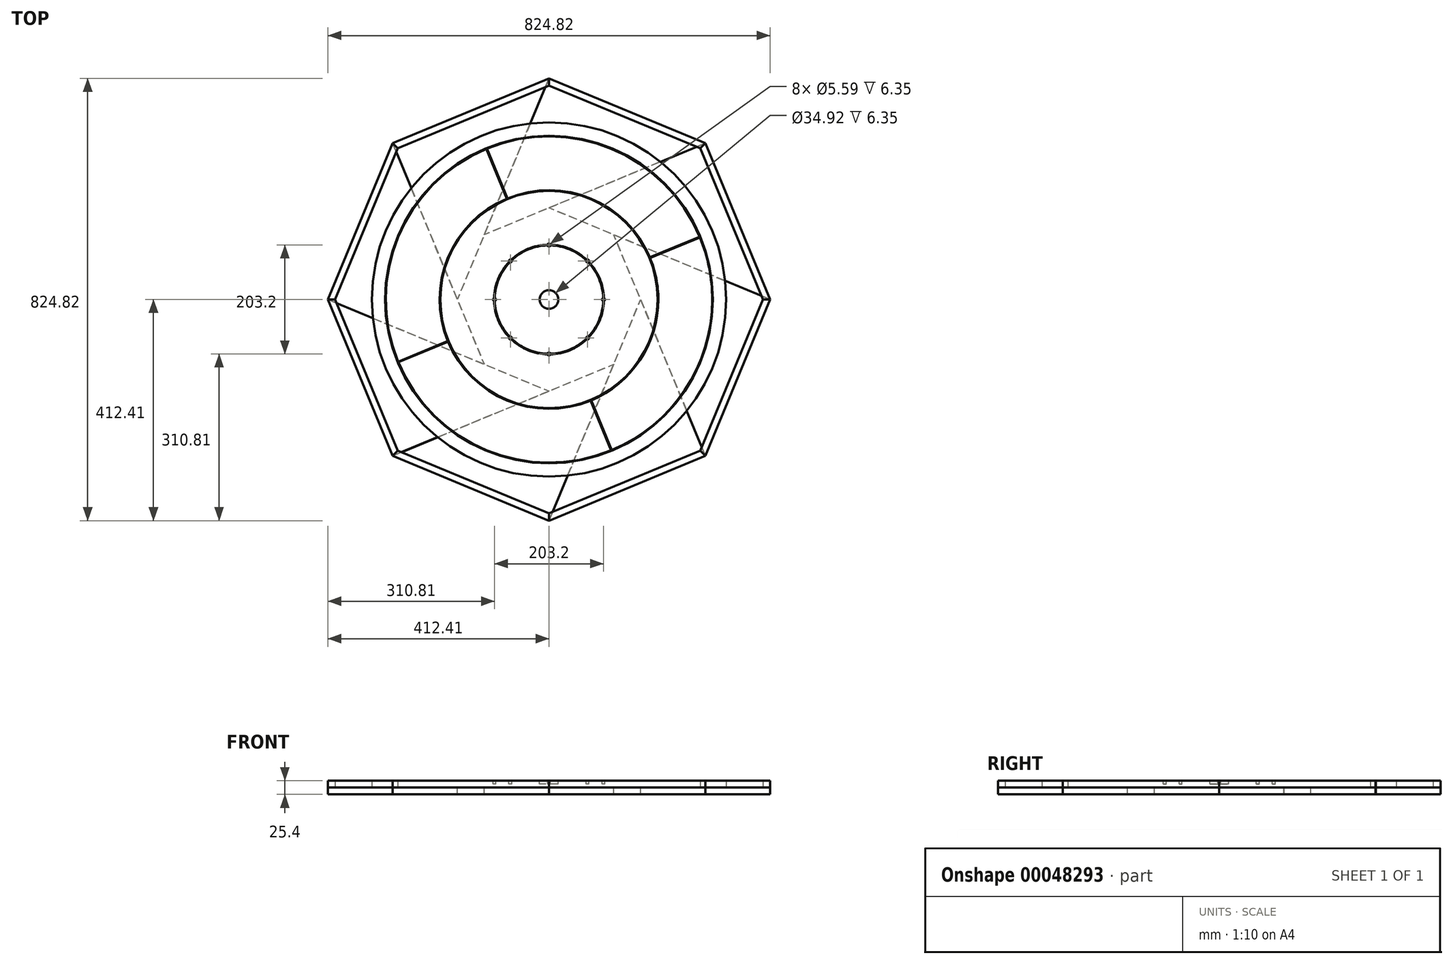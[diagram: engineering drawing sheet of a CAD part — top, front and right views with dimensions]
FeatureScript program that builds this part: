
annotation { "Feature Type Name" : "Feature", "Feature Type Description" : "" }
export const myFeature = defineFeature(function(context is Context, id is Id, definition is map)
    precondition{}
    {
        {
            var Q0;
            Q0=qCreatedBy(makeId("Top.planeOp"),FACE);
            var sketch = newSketch(context, id + "F0", { "sketchPlane" : qUnion([Q0])});
            skCircle(sketch, "E0", {"center": v(0, 0) * mm, "radius": 330.2 * mm});
            skSolve(sketch);
        }
        {
            var Q0;
            Q0=makeQuery(id+"F0.imprint","IMPRINT",FACE,{"disambiguationData":[TD([[makeQuery(id+"F0.imprint","IMPRINT",EDGE,{"derivedFrom":sQuery(id+"F0.wireOp",EDGE,"E0")}),1.0]])]});
            extrude(context, id + "F1", {"entities" : qUnion([Q0]), "depth" : 12.7 * mm});
        }
        {
            var Q0;
            Q0=makeQuery(id+"F1.opExtrude","CAP_FACE",FACE,{"disambiguationData":[OSD([sQuery(id+"F0.wireOp",EDGE,"E0")])],"isStart":false});
            var sketch = newSketch(context, id + "F2", { "sketchPlane" : qUnion([Q0])});
            skCircle(sketch, "E1", {"center": v(0, 0) * mm, "radius": 17.46 * mm});
            skSolve(sketch);
        }
        {
            var Q0;
            Q0 = qSketchRegion(id + "F2", true);
            extrude(context, id + "F3", {"entities" : qUnion([Q0]), "operationType" : NewBodyOperationType.REMOVE, "oppositeDirection" : true, "depth" : 6.35 * mm});
        }
        {
            var Q0;
            Q0=makeQuery(id+"F1.opExtrude","CAP_FACE",FACE,{"disambiguationData":[OSD([sQuery(id+"F0.wireOp",EDGE,"E0")])],"isStart":false});
            var sketch = newSketch(context, id + "F4", { "sketchPlane" : qUnion([Q0])});
            skCircle(sketch, "E2", {"center": v(101.6, 0) * mm, "radius": 2.8 * mm});
            skCircle(sketch, "E3.1.0", {"center": v(71.84, 71.84) * mm, "radius": 2.8 * mm});
            skCircle(sketch, "E3.2.0", {"center": v(0, 101.6) * mm, "radius": 2.8 * mm});
            skCircle(sketch, "E3.3.0", {"center": v(-71.84, 71.84) * mm, "radius": 2.8 * mm});
            skCircle(sketch, "E3.4.0", {"center": v(-101.6, 0) * mm, "radius": 2.8 * mm});
            skCircle(sketch, "E3.5.0", {"center": v(-71.84, -71.84) * mm, "radius": 2.8 * mm});
            skCircle(sketch, "E3.6.0", {"center": v(0, -101.6) * mm, "radius": 2.8 * mm});
            skCircle(sketch, "E3.7.0", {"center": v(71.84, -71.84) * mm, "radius": 2.8 * mm});
            skPoint(sketch, "E3.center", {"position": v(0, 0) * mm});
            skSolve(sketch);
        }
        {
            var Q0;
            Q0 = qSketchRegion(id + "F4", true);
            extrude(context, id + "F5", {"entities" : qUnion([Q0]), "operationType" : NewBodyOperationType.REMOVE, "oppositeDirection" : true, "depth" : 6.35 * mm});
        }
        {
            var Q0;
            Q0=qCreatedBy(makeId("Front.planeOp"),FACE);
            var sketch = newSketch(context, id + "F6", { "sketchPlane" : qUnion([Q0])});
            skArc(sketch, "E4", {"start": v(-102.24, 12.7) * mm, "mid": v(-101.6, 12.53) * mm, "end": v(-100.97, 12.7) * mm});
            skLineSegment(sketch, "E5", {"start": v(-102.24, 12.7) * mm, "end": v(-100.97, 12.7) * mm});
            skLineSegment(sketch, "E6", {"start": v(0, 0) * mm, "end": v(0, 26.45) * mm});
            skLineSegment(sketch, "E7.1.0.0", {"start": v(-203.84, 12.7) * mm, "end": v(-202.57, 12.7) * mm});
            skArc(sketch, "E7.1.0.1", {"start": v(-203.84, 12.7) * mm, "mid": v(-203.2, 12.53) * mm, "end": v(-202.57, 12.7) * mm});
            skLineSegment(sketch, "E7.direction1", {"start": v(-102.24, 12.7) * mm, "end": v(-203.84, 12.7) * mm, "construction": true});
            skLineSegment(sketch, "E8.0.2.0", {"start": v(-305.44, 12.7) * mm, "end": v(-304.17, 12.7) * mm});
            skArc(sketch, "E8.3.2.0", {"start": v(-305.44, 12.7) * mm, "mid": v(-304.8, 12.53) * mm, "end": v(-304.17, 12.7) * mm});
            skSolve(sketch);
        }
        {
            var Q0;
            Q0 = qSketchRegion(id + "F6", true);
            var Q1;
            Q1=sQuery(id+"F6.wireOp",EDGE,"E6");
            revolve(context, id + "F7", {"operationType" : NewBodyOperationType.REMOVE, "entities" : qUnion([Q0]), "axis" : qUnion([Q1]), "revolveType" : RevolveType.FULL, "oppositeDirection" : true});
        }
        {
            var Q0;
            Q0=makeQuery(id+"F5.boolean.opBoolean","COPY",FACE,{"derivedFrom":makeQuery(id+"F5.opExtrude","SWEPT_FACE",FACE,{"disambiguationData":[OSD([sQuery(id+"F4.wireOp",EDGE,"E3.3.0")])]})});
            var Q1;
            Q1=makeQuery(id+"F5.boolean.opBoolean","COPY",FACE,{"derivedFrom":makeQuery(id+"F5.opExtrude","SWEPT_FACE",FACE,{"disambiguationData":[OSD([sQuery(id+"F4.wireOp",EDGE,"E3.2.0")])]})});
            cPlane(context, id + "F8", {"entities" : qUnion([Q0, Q1]), "cplaneType" : CPlaneType.LINE_ANGLE, "offset" : 152.4 * mm, "angle" : 0 * degree, "width" : 152.4 * mm, "height" : 152.4 * mm});
        }
        {
            var Q0;
            Q0=makeQuery(id+"F7.boolean.opBoolean","SPLIT",FACE,{"disambiguationData":[TD([makeQuery(id+"F3.boolean.opBoolean","COPY",FACE,{"derivedFrom":makeQuery(id+"F3.opExtrude","SWEPT_FACE",FACE,{"disambiguationData":[OSD([sQuery(id+"F2.wireOp",EDGE,"E1")])]})}),makeQuery(id+"F5.boolean.opBoolean","COPY",FACE,{"derivedFrom":makeQuery(id+"F5.opExtrude","SWEPT_FACE",FACE,{"disambiguationData":[OSD([sQuery(id+"F4.wireOp",EDGE,"E2")])]})}),makeQuery(id+"F5.boolean.opBoolean","COPY",FACE,{"derivedFrom":makeQuery(id+"F5.opExtrude","SWEPT_FACE",FACE,{"disambiguationData":[OSD([sQuery(id+"F4.wireOp",EDGE,"E3.1.0")])]})}),makeQuery(id+"F5.boolean.opBoolean","COPY",FACE,{"derivedFrom":makeQuery(id+"F5.opExtrude","SWEPT_FACE",FACE,{"disambiguationData":[OSD([sQuery(id+"F4.wireOp",EDGE,"E3.2.0")])]})}),makeQuery(id+"F5.boolean.opBoolean","COPY",FACE,{"derivedFrom":makeQuery(id+"F5.opExtrude","SWEPT_FACE",FACE,{"disambiguationData":[OSD([sQuery(id+"F4.wireOp",EDGE,"E3.3.0")])]})}),makeQuery(id+"F5.boolean.opBoolean","COPY",FACE,{"derivedFrom":makeQuery(id+"F5.opExtrude","SWEPT_FACE",FACE,{"disambiguationData":[OSD([sQuery(id+"F4.wireOp",EDGE,"E3.4.0")])]})}),makeQuery(id+"F5.boolean.opBoolean","COPY",FACE,{"derivedFrom":makeQuery(id+"F5.opExtrude","SWEPT_FACE",FACE,{"disambiguationData":[OSD([sQuery(id+"F4.wireOp",EDGE,"E3.5.0")])]})}),makeQuery(id+"F5.boolean.opBoolean","COPY",FACE,{"derivedFrom":makeQuery(id+"F5.opExtrude","SWEPT_FACE",FACE,{"disambiguationData":[OSD([sQuery(id+"F4.wireOp",EDGE,"E3.6.0")])]})}),makeQuery(id+"F5.boolean.opBoolean","COPY",FACE,{"derivedFrom":makeQuery(id+"F5.opExtrude","SWEPT_FACE",FACE,{"disambiguationData":[OSD([sQuery(id+"F4.wireOp",EDGE,"E3.7.0")])]})}),makeQuery(id+"F7.opRevolve","SWEPT_FACE",FACE,{"disambiguationData":[OSD([sQuery(id+"F6.wireOp",EDGE,"E4")])]})])],"derivedFrom":makeQuery(id+"F1.opExtrude","CAP_FACE",FACE,{"disambiguationData":[OSD([sQuery(id+"F0.wireOp",EDGE,"E0")])],"isStart":false})});
            var sketch = newSketch(context, id + "F9", { "sketchPlane" : qUnion([Q0])});
            skLineSegment(sketch, "E9", {"start": v(0, 0) * mm, "end": v(-110.78, 267.45) * mm});
            skLineSegment(sketch, "E10", {"start": v(-78, 188.32) * mm, "end": v(-110.7, 174.78) * mm});
            skLineSegment(sketch, "E11", {"start": v(-78, 188.32) * mm, "end": v(-71.84, 71.84) * mm});
            skLineSegment(sketch, "E12", {"start": v(0, 101.6) * mm, "end": v(-78, 188.32) * mm});
            skSolve(sketch);
        }
        {
            var Q0;
            Q0=qCreatedBy(id+"F8.planeOp",FACE);
            var Q1;
            Q1=sQuery(id+"F9.wireOp",VERTEX,"E10.end");
            cPlane(context, id + "F10", {"entities" : qUnion([Q0, Q1]), "cplaneType" : CPlaneType.PLANE_POINT, "offset" : 152.4 * mm, "width" : 152.4 * mm, "height" : 152.4 * mm});
        }
        {
            var Q0;
            Q0=qCreatedBy(id+"F10.planeOp",FACE);
            var sketch = newSketch(context, id + "F11", { "sketchPlane" : qUnion([Q0])});
            skArc(sketch, "E13", {"start": v(-0.63, 12.7) * mm, "mid": v(0, 12.53) * mm, "end": v(0.64, 12.7) * mm});
            skLineSegment(sketch, "E14", {"start": v(-0.63, 12.7) * mm, "end": v(0.64, 12.7) * mm});
            skSolve(sketch);
        }
        {
            var Q0;
            Q0 = qSketchRegion(id + "F11", true);
            extrude(context, id + "F12", {"entities" : qUnion([Q0]), "operationType" : NewBodyOperationType.REMOVE, "oppositeDirection" : true, "depth" : 100.56 * mm});
        }
        {
            var Q0;
            Q0=makeQuery(id+"F12.boolean.opBoolean","COPY",FACE,{"derivedFrom":makeQuery(id+"F12.opExtrude","SWEPT_FACE",FACE,{"disambiguationData":[OSD([sQuery(id+"F11.wireOp",EDGE,"E13")])]})});
            var Q1;
            Q1=makeQuery(id+"F12.boolean.opBoolean","COPY",FACE,{"derivedFrom":makeQuery(id+"F12.opExtrude","CAP_FACE",FACE,{"disambiguationData":[OSD([sQuery(id+"F11.wireOp",EDGE,"E13"),sQuery(id+"F11.wireOp",EDGE,"E14")])],"isStart":false})});
            var Q2;
            Q2=makeQuery(id+"F12.boolean.opBoolean","COPY",FACE,{"derivedFrom":makeQuery(id+"F12.opExtrude","CAP_FACE",FACE,{"disambiguationData":[OSD([sQuery(id+"F11.wireOp",EDGE,"E13"),sQuery(id+"F11.wireOp",EDGE,"E14")])],"isStart":true})});
            var Q3;
            Q3=makeQuery(id+"F1.opExtrude","CAP_EDGE",EDGE,{"disambiguationData":[OSD([sQuery(id+"F0.wireOp",EDGE,"E0")])],"isStart":false});
            circularPattern(context, id + "F13", {"faces" : qUnion([Q0, Q1, Q2]), "axis" : qUnion([Q3]), "angle" : 360 * degree, "instanceCount" : 4, "equalSpace" : true, "patternType" : PatternType.FACE});
        }
        {
            var Q0;
            Q0=makeQuery(id+"F1.opExtrude","CAP_FACE",FACE,{"disambiguationData":[OSD([sQuery(id+"F0.wireOp",EDGE,"E0")])],"isStart":true});
            var sketch = newSketch(context, id + "F14", { "sketchPlane" : qUnion([Q0])});
            skLineSegment(sketch, "E15", {"start": v(-291.65, -291.59) * mm, "end": v(0.04, -412.4) * mm});
            skLineSegment(sketch, "E16", {"start": v(0.04, -412.4) * mm, "end": v(-170.83, 0.1) * mm});
            skLineSegment(sketch, "E17", {"start": v(-170.83, 0.1) * mm, "end": v(-291.65, -291.59) * mm});
            skLineSegment(sketch, "E18", {"start": v(-145.8, -352) * mm, "end": v(-126.36, -305.07) * mm});
            skSolve(sketch);
        }
        {
            var Q0;
            {var subQ3=sQuery(id+"F14.wireOp",EDGE,"E18");Q0=makeQuery(id+"F14.imprint","IMPRINT",FACE,{"disambiguationData":[TD([[makeQuery(id+"F14.imprint","IMPRINT",EDGE,{"derivedFrom":subQ3}),1.0]])]});}
            var Q1;
            {var subQ1=sQuery(id+"F14.wireOp",EDGE,"E17");var subQ4=sQuery(id+"F14.wireOp",EDGE,"E16");var subQ6=makeQuery(id+"F14.imprint","INTERSECT",VERTEX,{"derivedFrom":[subQ4,subQ1]});Q1=makeQuery(id+"F14.imprint","IMPRINT",FACE,{"disambiguationData":[TD([[makeQuery(id+"F14.imprint","IMPRINT",EDGE,{"disambiguationData":[TD([[subQ6,1.0]])],"derivedFrom":subQ4}),1.0]])]});}
            var Q2;
            {var subQ3=sQuery(id+"F14.wireOp",EDGE,"E18");Q2=makeQuery(id+"F14.imprint","IMPRINT",FACE,{"disambiguationData":[TD([[makeQuery(id+"F14.imprint","IMPRINT",EDGE,{"derivedFrom":subQ3}),-1.0]])]});}
            extrude(context, id + "F15", {"entities" : qUnion([Q0, Q1, Q2]), "depth" : 12.7 * mm});
        }
        {
            var Q0;
            Q0=makeQuery(id+"F15.opExtrude","SWEPT_BODY",BODY,{"disambiguationData":[OSD([sQuery(id+"F14.wireOp",EDGE,"E15"),sQuery(id+"F14.wireOp",EDGE,"E16"),sQuery(id+"F14.wireOp",EDGE,"E17")])]});
            var Q1;
            Q1=makeQuery(id+"F1.opExtrude","SWEPT_FACE",FACE,{"disambiguationData":[OSD([sQuery(id+"F0.wireOp",EDGE,"E0")])]});
            circularPattern(context, id + "F16", {"entities" : qUnion([Q0]), "axis" : qUnion([Q1]), "angle" : 360 * degree, "instanceCount" : 8, "equalSpace" : true});
        }
        {
            var Q0;
            Q0=makeQuery(id+"F16.opPattern","COPY",FACE,{"derivedFrom":makeQuery(id+"F15.opExtrude","CAP_FACE",FACE,{"disambiguationData":[OSD([sQuery(id+"F14.wireOp",EDGE,"E15"),sQuery(id+"F14.wireOp",EDGE,"E16"),sQuery(id+"F14.wireOp",EDGE,"E17")])],"isStart":true}),"instanceName":"7"});
            var sketch = newSketch(context, id + "F17", { "sketchPlane" : qUnion([Q0])});
            skLineSegment(sketch, "E19", {"start": v(-412.4, -0.04) * mm, "end": v(-398.66, -0.04) * mm});
            skLineSegment(sketch, "E20", {"start": v(-398.66, -0.04) * mm, "end": v(-281.87, 281.93) * mm});
            skLineSegment(sketch, "E21", {"start": v(-281.87, 281.93) * mm, "end": v(-291.59, 291.65) * mm});
            skLineSegment(sketch, "E22", {"start": v(-291.59, 291.65) * mm, "end": v(-412.4, -0.04) * mm});
            skSolve(sketch);
        }
        {
            var Q0;
            {var subQ4=sQuery(id+"F17.wireOp",EDGE,"E19");Q0=makeQuery(id+"F17.imprint","IMPRINT",FACE,{"disambiguationData":[TD([[makeQuery(id+"F17.imprint","IMPRINT",EDGE,{"derivedFrom":subQ4}),1.0]])]});}
            var Q1;
            {var subQ3=sQuery(id+"F17.wireOp",EDGE,"E21");Q1=makeQuery(id+"F17.imprint","IMPRINT",FACE,{"disambiguationData":[TD([[makeQuery(id+"F17.imprint","IMPRINT",EDGE,{"derivedFrom":subQ3}),1.0]])]});}
            extrude(context, id + "F18", {"entities" : qUnion([Q0, Q1]), "depth" : 12.7 * mm});
        }
        {
            var Q0;
            Q0=makeQuery(id+"F18.opExtrude","SWEPT_BODY",BODY,{"disambiguationData":[OSD([sQuery(id+"F17.wireOp",EDGE,"E19"),sQuery(id+"F17.wireOp",EDGE,"E20"),sQuery(id+"F17.wireOp",EDGE,"E21"),sQuery(id+"F17.wireOp",EDGE,"E22")])]});
            var Q1;
            Q1=makeQuery(id+"F1.opExtrude","SWEPT_FACE",FACE,{"disambiguationData":[OSD([sQuery(id+"F0.wireOp",EDGE,"E0")])]});
            circularPattern(context, id + "F19", {"entities" : qUnion([Q0]), "axis" : qUnion([Q1]), "angle" : 360 * degree, "instanceCount" : 8, "equalSpace" : true});
        }
    });
